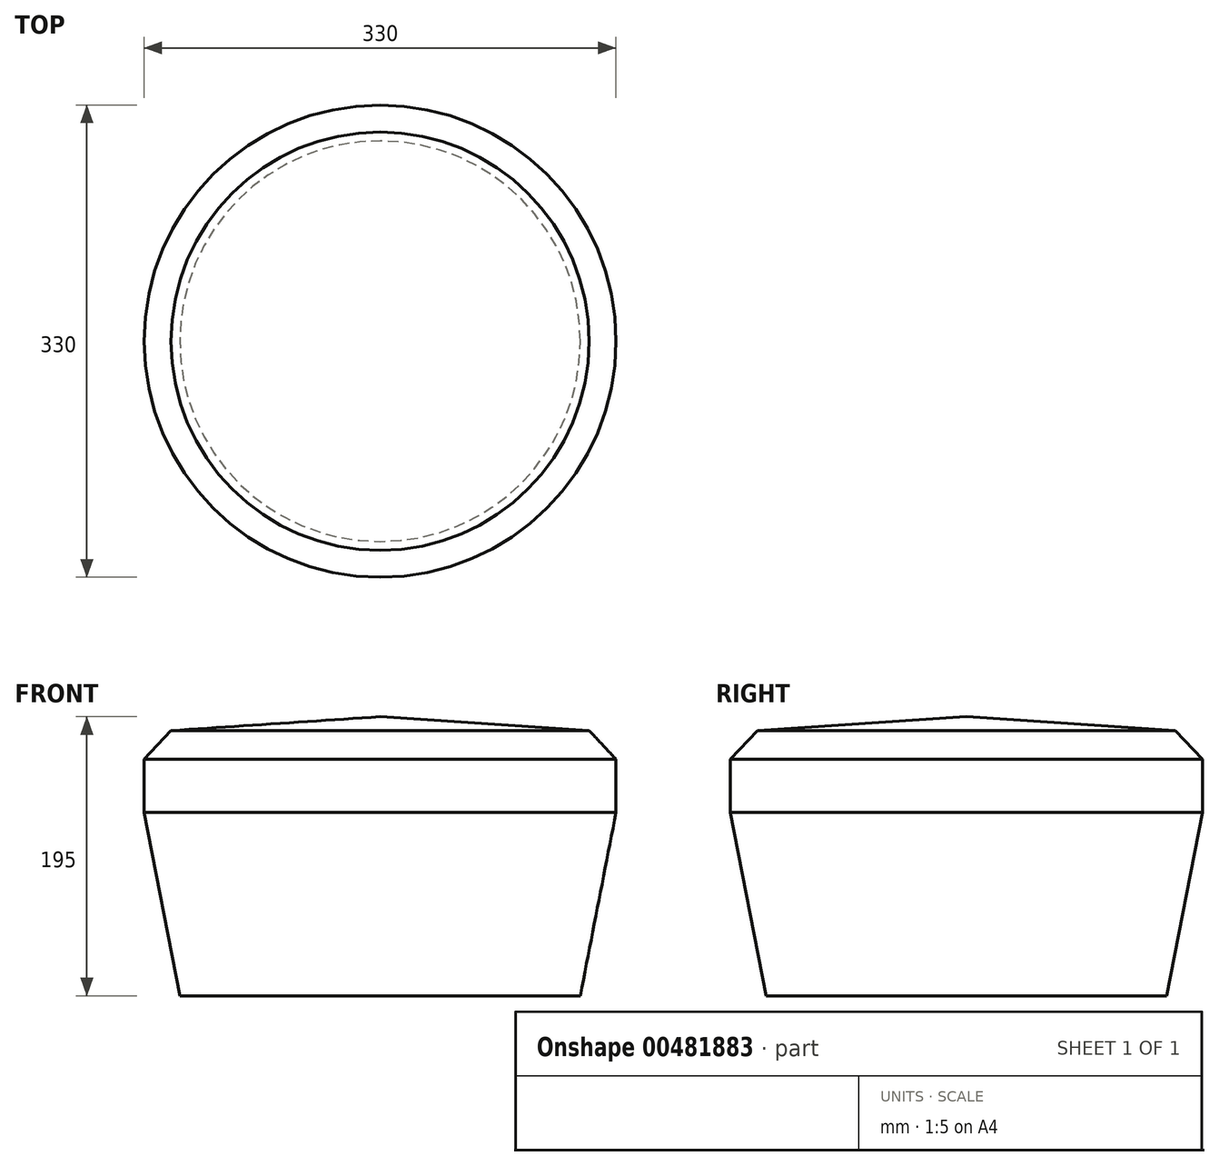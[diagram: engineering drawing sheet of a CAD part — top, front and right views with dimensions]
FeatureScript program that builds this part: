
annotation { "Feature Type Name" : "Feature", "Feature Type Description" : "" }
export const myFeature = defineFeature(function(context is Context, id is Id, definition is map)
    precondition{}
    {
        {
            var Q0;
            Q0=qCreatedBy(makeId("Front.planeOp"),FACE);
            var sketch = newSketch(context, id + "F0", { "sketchPlane" : qUnion([Q0])});
            skLineSegment(sketch, "E0", {"start": v(0, 0) * mm, "end": v(0, 195) * mm});
            skLineSegment(sketch, "E1", {"start": v(0, 195) * mm, "end": v(0, 0) * mm});
            skLineSegment(sketch, "E2", {"start": v(-140, 0) * mm, "end": v(-165, 128.28) * mm});
            skLineSegment(sketch, "E3", {"start": v(-165, 128.28) * mm, "end": v(-165, 165.28) * mm});
            skLineSegment(sketch, "E4", {"start": v(-165, 165.28) * mm, "end": v(-146.2, 185.3) * mm});
            skLineSegment(sketch, "E5", {"start": v(-146.2, 185.3) * mm, "end": v(0, 195) * mm});
            skLineSegment(sketch, "E6", {"start": v(0, 0) * mm, "end": v(-140, 0) * mm});
            skSolve(sketch);
        }
        {
            var Q0;
            Q0 = qSketchRegion(id + "F0", true);
            var Q1;
            Q1=sQuery(id+"F0.wireOp",EDGE,"E1");
            revolve(context, id + "F1", {"entities" : qUnion([Q0]), "axis" : qUnion([Q1]), "revolveType" : RevolveType.FULL});
        }
    });
